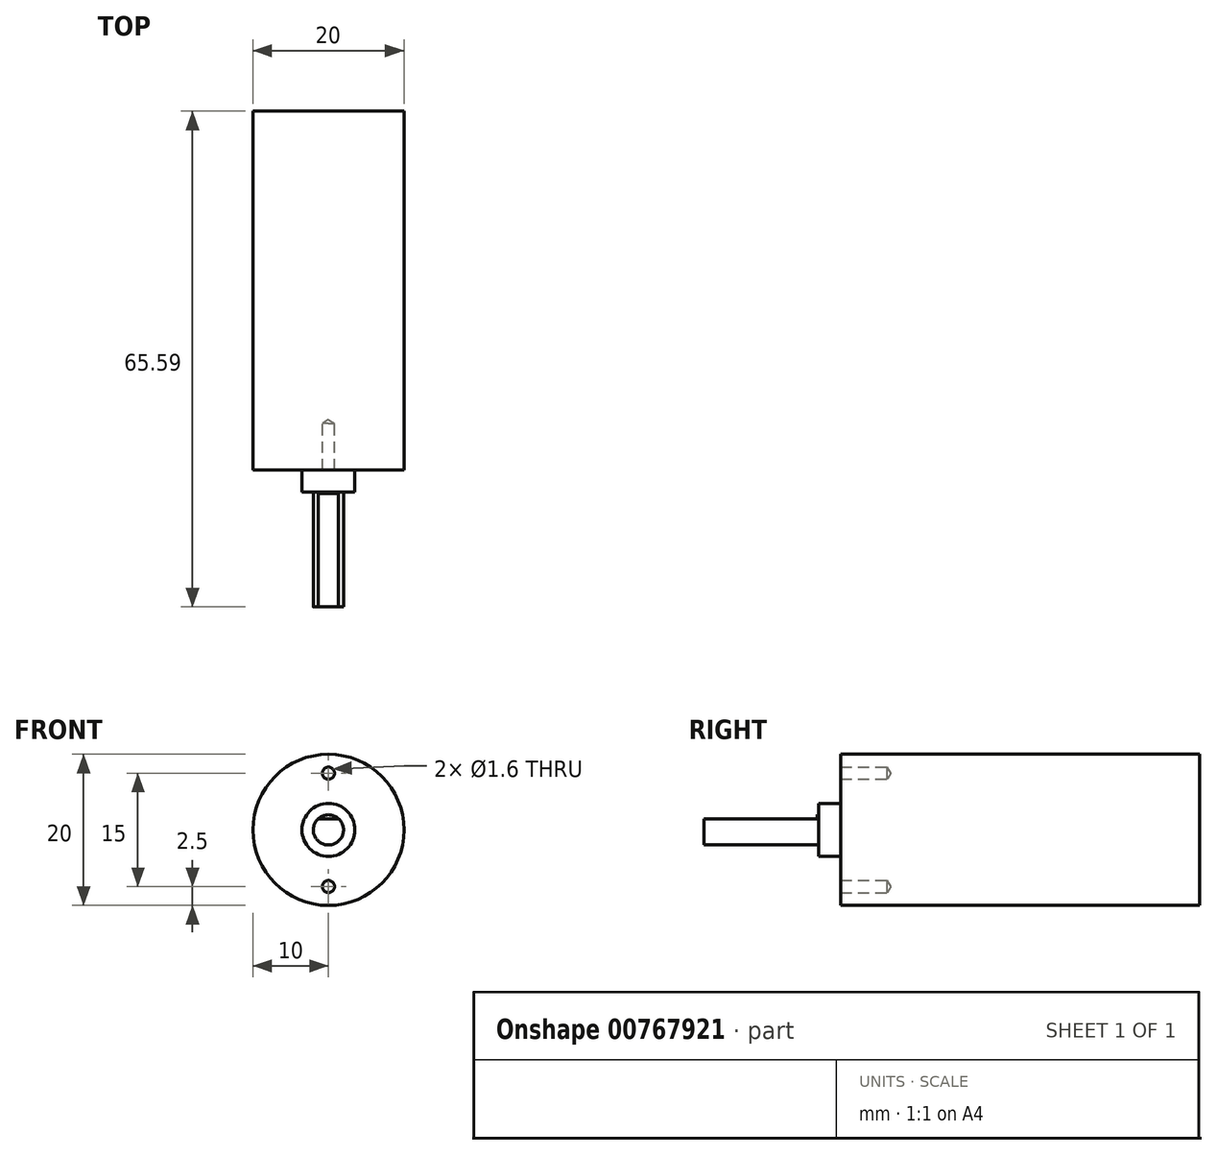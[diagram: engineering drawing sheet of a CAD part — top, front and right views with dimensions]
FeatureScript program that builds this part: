
annotation { "Feature Type Name" : "Feature", "Feature Type Description" : "" }
export const myFeature = defineFeature(function(context is Context, id is Id, definition is map)
    precondition{}
    {
        {
            var Q0;
            Q0=qCreatedBy(makeId("Front.planeOp"),FACE);
            var sketch = newSketch(context, id + "F0", { "sketchPlane" : qUnion([Q0])});
            skCircle(sketch, "E0", {"center": v(0, 0) * mm, "radius": 10 * mm});
            skSolve(sketch);
        }
        {
            var Q0;
            Q0=makeQuery(id+"F0.imprint","IMPRINT",FACE,{"disambiguationData":[TD([[makeQuery(id+"F0.imprint","IMPRINT",EDGE,{"derivedFrom":sQuery(id+"F0.wireOp",EDGE,"E0")}),1.0]])]});
            extrude(context, id + "F1", {"entities" : qUnion([Q0]), "depth" : (20.3 + 27.2) * mm, "offsetDistance" : 25 * mm});
        }
        {
            var Q0;
            Q0=makeQuery(id+"F1.opExtrude","CAP_FACE",FACE,{"disambiguationData":[OSD([sQuery(id+"F0.wireOp",EDGE,"E0")])],"isStart":false});
            var sketch = newSketch(context, id + "F2", { "sketchPlane" : qUnion([Q0])});
            skCircle(sketch, "E1", {"center": v(0, 0) * mm, "radius": 3.5 * mm});
            skSolve(sketch);
        }
        {
            var Q0;
            Q0=makeQuery(id+"F2.imprint","IMPRINT",FACE,{"disambiguationData":[TD([[makeQuery(id+"F2.imprint","IMPRINT",EDGE,{"derivedFrom":sQuery(id+"F2.wireOp",EDGE,"E1")}),1.0]])]});
            extrude(context, id + "F3", {"entities" : qUnion([Q0]), "operationType" : NewBodyOperationType.ADD, "depth" : 2.9 * mm, "offsetDistance" : 25 * mm});
        }
        {
            var Q0;
            Q0=makeQuery(id+"F3.opExtrude","CAP_FACE",FACE,{"disambiguationData":[OSD([sQuery(id+"F2.wireOp",EDGE,"E1")])],"isStart":false});
            var sketch = newSketch(context, id + "F4", { "sketchPlane" : qUnion([Q0])});
            skCircle(sketch, "E2", {"center": v(0, 0) * mm, "radius": 2 * mm});
            skSolve(sketch);
        }
        {
            var Q0;
            Q0=makeQuery(id+"F4.imprint","IMPRINT",FACE,{"disambiguationData":[TD([[makeQuery(id+"F4.imprint","IMPRINT",EDGE,{"derivedFrom":sQuery(id+"F4.wireOp",EDGE,"E2")}),1.0]])]});
            extrude(context, id + "F5", {"entities" : qUnion([Q0]), "operationType" : NewBodyOperationType.ADD, "depth" : 15.2 * mm, "offsetDistance" : 25 * mm});
        }
        {
            var Q0;
            Q0=makeQuery(id+"F1.opExtrude","CAP_FACE",FACE,{"disambiguationData":[OSD([sQuery(id+"F0.wireOp",EDGE,"E0")])],"isStart":false});
            var sketch = newSketch(context, id + "F6", { "sketchPlane" : qUnion([Q0])});
            skCircle(sketch, "E3", {"center": v(0, 0) * mm, "radius": 7.5 * mm, "construction": true});
            skCircle(sketch, "E4", {"center": v(0, 7.5) * mm, "radius": 1 * mm});
            skCircle(sketch, "E5", {"center": v(0, -7.5) * mm, "radius": 1 * mm});
            skSolve(sketch);
        }
        {
            var Q0;
            Q0=sQuery(id+"F6.wireOp",VERTEX,"E4.center");
            var Q1;
            Q1=sQuery(id+"F6.wireOp",VERTEX,"E5.center");
            var Q2;
            Q2=makeQuery(id+"F1.opExtrude","SWEPT_BODY",BODY,{"disambiguationData":[OSD([sQuery(id+"F0.wireOp",EDGE,"E0")])]});
            hole(context, id + "F7", {"style" : HoleStyle.SIMPLE, "endStyle" : HoleEndStyle.BLIND, "standardTappedOrClearance" : lookupTablePath({ "standard" : "ISO", "engagement" : "75%", "pitch" : "0.4 mm", "size" : "M2", "type" : "Tapped" }), "standardBlindInLast" : lookupTablePath({ "standard" : "ISO", "fit" : "Normal", "engagement" : "75%", "pitch" : "0.4 mm", "size" : "M2", "type" : "Clearance & tapped" }), "holeDiameter" : 1.6 * mm, "majorDiameter" : 2 * mm, "showTappedDepth" : true, "holeDepth" : 6.2 * mm, "tappedDepth" : 5 * mm, "tapClearance" : 3, "locations" : qUnion([Q0, Q1]), "scope" : qUnion([Q2])});
        }
        {
            var Q0;
            Q0=makeQuery(id+"F5.opExtrude","CAP_FACE",FACE,{"disambiguationData":[OSD([sQuery(id+"F4.wireOp",EDGE,"E2")])],"isStart":false});
            var sketch = newSketch(context, id + "F8", { "sketchPlane" : qUnion([Q0])});
            skLineSegment(sketch, "E6", {"start": v(-1.34, 1.48) * mm, "end": v(1.34, 1.48) * mm});
            skSolve(sketch);
        }
        {
            var Q0;
            {var subQ0=sQuery(id+"F8.wireOp",EDGE,"E6");Q0=makeQuery(id+"F8.imprint","IMPRINT",FACE,{"disambiguationData":[TD([[makeQuery(id+"F8.imprint","IMPRINT",EDGE,{"derivedFrom":subQ0}),1.0]])]});}
            extrude(context, id + "F9", {"entities" : qUnion([Q0]), "operationType" : NewBodyOperationType.REMOVE, "oppositeDirection" : true, "depth" : 15 * mm, "offsetDistance" : 25 * mm});
        }
    });
